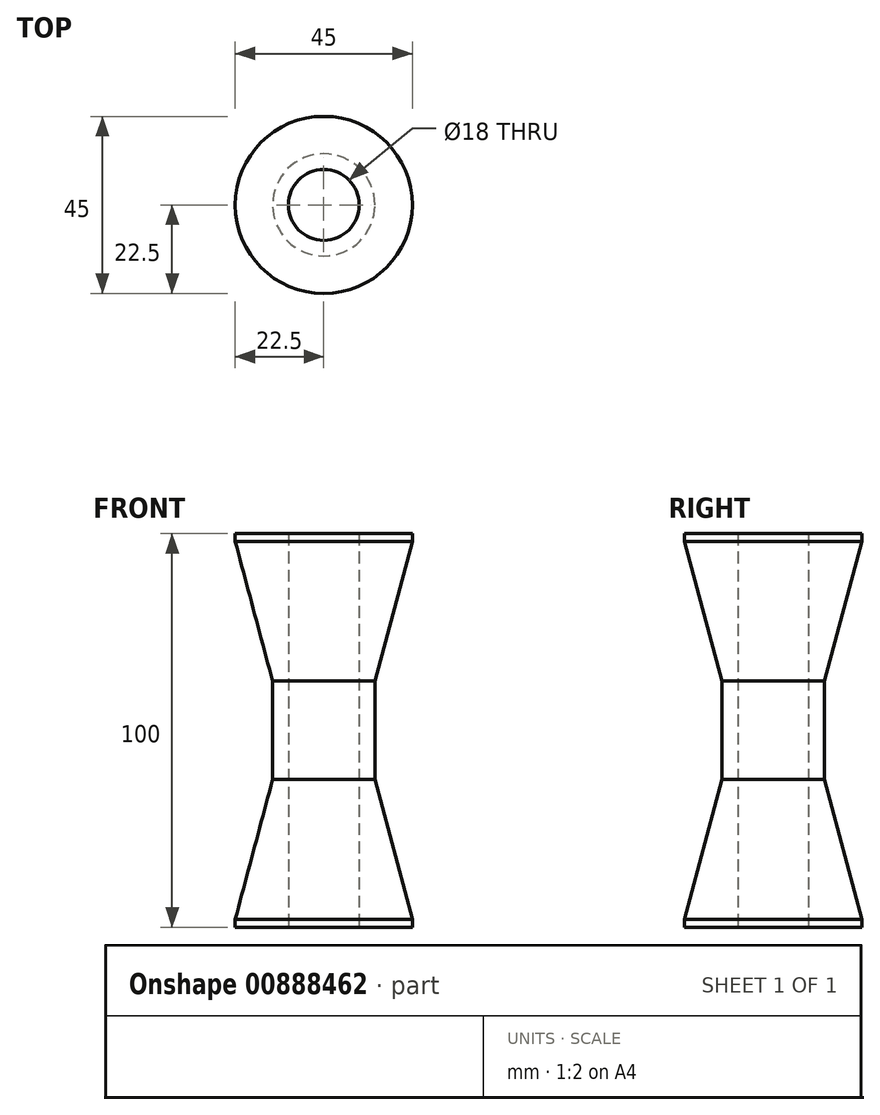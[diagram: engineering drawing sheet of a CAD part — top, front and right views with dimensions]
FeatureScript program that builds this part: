
annotation { "Feature Type Name" : "Feature", "Feature Type Description" : "" }
export const myFeature = defineFeature(function(context is Context, id is Id, definition is map)
    precondition{}
    {
        {
            var Q0;
            Q0=qCreatedBy(makeId("Right.planeOp"),FACE);
            var sketch = newSketch(context, id + "F0", { "sketchPlane" : qUnion([Q0])});
            skLineSegment(sketch, "E0", {"start": v(9, 0) * mm, "end": v(22.5, 0) * mm});
            skLineSegment(sketch, "E1", {"start": v(22.5, 0) * mm, "end": v(22.5, 2) * mm});
            skLineSegment(sketch, "E2", {"start": v(22.5, 2) * mm, "end": v(12.99, 37.5) * mm});
            skLineSegment(sketch, "E3", {"start": v(12.99, 37.5) * mm, "end": v(12.99, 62.5) * mm});
            skLineSegment(sketch, "E4", {"start": v(12.99, 62.5) * mm, "end": v(22.5, 98) * mm});
            skLineSegment(sketch, "E5", {"start": v(22.5, 98) * mm, "end": v(22.5, 100) * mm});
            skLineSegment(sketch, "E6", {"start": v(22.5, 100) * mm, "end": v(9, 100) * mm});
            skLineSegment(sketch, "E7", {"start": v(9, 100) * mm, "end": v(9, 0) * mm});
            skLineSegment(sketch, "E8", {"start": v(0, 0) * mm, "end": v(0, 113.86) * mm, "construction": true});
            skLineSegment(sketch, "E9", {"start": v(9, 50) * mm, "end": v(23.98, 50) * mm, "construction": true});
            skSolve(sketch);
        }
        {
            var Q0;
            Q0=makeQuery(id+"F0.imprint","IMPRINT",FACE,{"disambiguationData":[TD([[makeQuery(id+"F0.imprint","IMPRINT",EDGE,{"derivedFrom":sQuery(id+"F0.wireOp",EDGE,"E0")}),1.0]])]});
            var Q1;
            Q1=sQuery(id+"F0.wireOp",EDGE,"E8");
            revolve(context, id + "F1", {"surfaceOperationType" : NewSurfaceOperationType.NEW, "entities" : qUnion([Q0]), "axis" : qUnion([Q1]), "revolveType" : RevolveType.FULL});
        }
    });
